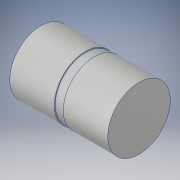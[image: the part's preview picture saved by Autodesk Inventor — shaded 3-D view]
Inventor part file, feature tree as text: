
AUTODESK INVENTOR PART (.ipt)
format: ipt  version: 2019 (Build 230136000, 136)  size: 221,184 bytes
history: native  units: mm
features: revolve x1, sketch x1
ambient origin geometry x8: Origin, YZ Plane, XZ Plane, XY Plane, X Axis, Y Axis, Z Axis, Center Point
bodies: Solid1 (feature_tree)
feature tree (2):
  revolve  "Revolution1"  [1 undecoded]
  sketch  "Sketch1"  dims[d1=1.0mm d2=10.0mm d3=50.0mm d4=50.0mm d5=1.0mm d8=2.5mm d9=35.0mm d10=30.0mm d12=30.0mm d13=90.0deg d14=110.0mm]
note: 1 required parameter value undecoded (feature->parameter linkage not recoverable at this tier; creation-order binding heuristic only, values carry confidence <= 0.55)
